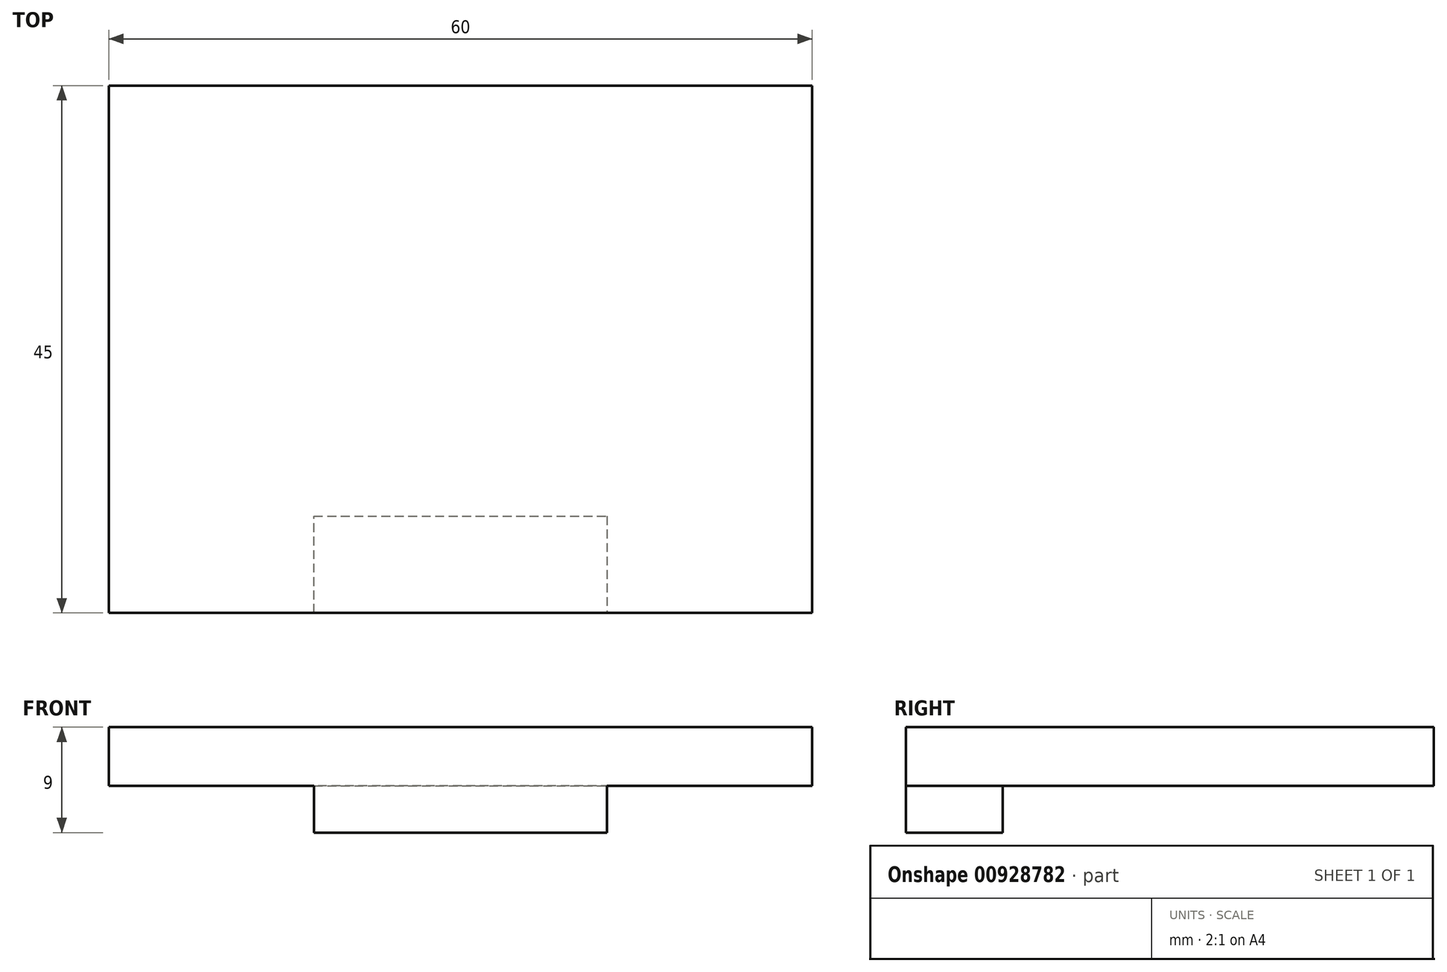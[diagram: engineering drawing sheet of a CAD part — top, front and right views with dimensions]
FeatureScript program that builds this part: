
annotation { "Feature Type Name" : "Feature", "Feature Type Description" : "" }
export const myFeature = defineFeature(function(context is Context, id is Id, definition is map)
    precondition{}
    {
        {
            var Q0;
            Q0=qCreatedBy(makeId("Top.planeOp"),FACE);
            var sketch = newSketch(context, id + "F0", { "sketchPlane" : qUnion([Q0])});
            skLineSegment(sketch, "E0.bottom", {"start": v(30, 22.5) * mm, "end": v(-30, 22.5) * mm});
            skLineSegment(sketch, "E0.top", {"start": v(30, -22.5) * mm, "end": v(-30, -22.5) * mm});
            skLineSegment(sketch, "E0.left", {"start": v(30, 22.5) * mm, "end": v(30, -22.5) * mm});
            skLineSegment(sketch, "E0.right", {"start": v(-30, 22.5) * mm, "end": v(-30, -22.5) * mm});
            skPoint(sketch, "E0.middle", {"position": v(0, 0) * mm});
            skSolve(sketch);
        }
        {
            var Q0;
            Q0=makeQuery(id+"F0.imprint","IMPRINT",FACE,{"disambiguationData":[TD([[makeQuery(id+"F0.imprint","IMPRINT",EDGE,{"derivedFrom":sQuery(id+"F0.wireOp",EDGE,"E0.bottom")}),1.0]])]});
            extrude(context, id + "F1", {"entities" : qUnion([Q0]), "depth" : 5 * mm, "offsetDistance" : 25 * mm});
        }
        {
            var Q0;
            Q0=makeQuery(id+"F1.opExtrude","CAP_FACE",FACE,{"disambiguationData":[OSD([sQuery(id+"F0.wireOp",EDGE,"E0.bottom"),sQuery(id+"F0.wireOp",EDGE,"E0.top"),sQuery(id+"F0.wireOp",EDGE,"E0.left"),sQuery(id+"F0.wireOp",EDGE,"E0.right")])],"isStart":true});
            var sketch = newSketch(context, id + "F2", { "sketchPlane" : qUnion([Q0])});
            skLineSegment(sketch, "E1.bottom", {"start": v(-12.35, -22.5) * mm, "end": v(30.15, -22.5) * mm});
            skLineSegment(sketch, "E1.top", {"start": v(-12.35, -14.25) * mm, "end": v(12.65, -14.25) * mm});
            skLineSegment(sketch, "E1.left", {"start": v(-12.35, -22.5) * mm, "end": v(-12.35, -14.25) * mm});
            skLineSegment(sketch, "E1.right", {"start": v(12.65, -22.5) * mm, "end": v(12.65, -14.25) * mm});
            skLineSegment(sketch, "E2.bottom", {"start": v(-12.5, 22.5) * mm, "end": v(30, 22.5) * mm});
            skLineSegment(sketch, "E2.top", {"start": v(-12.5, 14.25) * mm, "end": v(12.5, 14.25) * mm});
            skLineSegment(sketch, "E2.left", {"start": v(-12.5, 22.5) * mm, "end": v(-12.5, 14.25) * mm});
            skLineSegment(sketch, "E2.right", {"start": v(30, 22.5) * mm, "end": v(30, 14.25) * mm});
            skLineSegment(sketch, "E3", {"start": v(12.5, 14.25) * mm, "end": v(12.5, 22.5) * mm});
            skPoint(sketch, "E3.endSnap0", {"position": v(8.75, 22.5) * mm});
            skSolve(sketch);
        }
        {
            var Q0;
            Q0=makeQuery(id+"F2.imprint","IMPRINT",FACE,{"disambiguationData":[TD([[makeQuery(id+"F2.imprint","IMPRINT",EDGE,{"derivedFrom":sQuery(id+"F2.wireOp",EDGE,"E2.top")}),1.0]])]});
            extrude(context, id + "F3", {"entities" : qUnion([Q0]), "operationType" : NewBodyOperationType.ADD, "depth" : 4 * mm, "offsetDistance" : 25 * mm});
        }
    });
